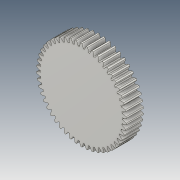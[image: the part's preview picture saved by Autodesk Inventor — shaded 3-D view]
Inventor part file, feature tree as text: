
AUTODESK INVENTOR PART (.ipt)
format: ipt  version: 2021 (Build 250183000, 183)  size: 330,752 bytes
history: native  units: mm (DEFAULTED — no unit token found)
features: plane x3, other x3, sketch x2, extrude x1
ambient origin geometry x8: Origin, YZ Plane, XZ Plane, XY Plane, X Axis, Y Axis, Z Axis, Center Point
bodies: Solid1 (feature_tree)
feature tree (9):
  extrude  "Extrusion1"  Depth=2.0mm TaperAngle=0.0deg
  plane  "Work Plane2"
  plane  "Work Plane8"
  plane  "Work Plane9"
  other  "Engrenagem reta"
  sketch  "Sketch1"  dims[d0=10.4mm d1=2.0mm d2=0.0mm]
  sketch  "Sketch2"  dims[d3=10.0mm d4=10.0mm d5=0.0mm d16=10.7mm d17=0.0mm d34=0.628319mm d39=0.0mm d41=0.0mm d43=10.7mm d46=10.7mm d47=0.0mm d48=0.0mm]
  other  "Srf1"
  other  "Diâmetro do flanco"
